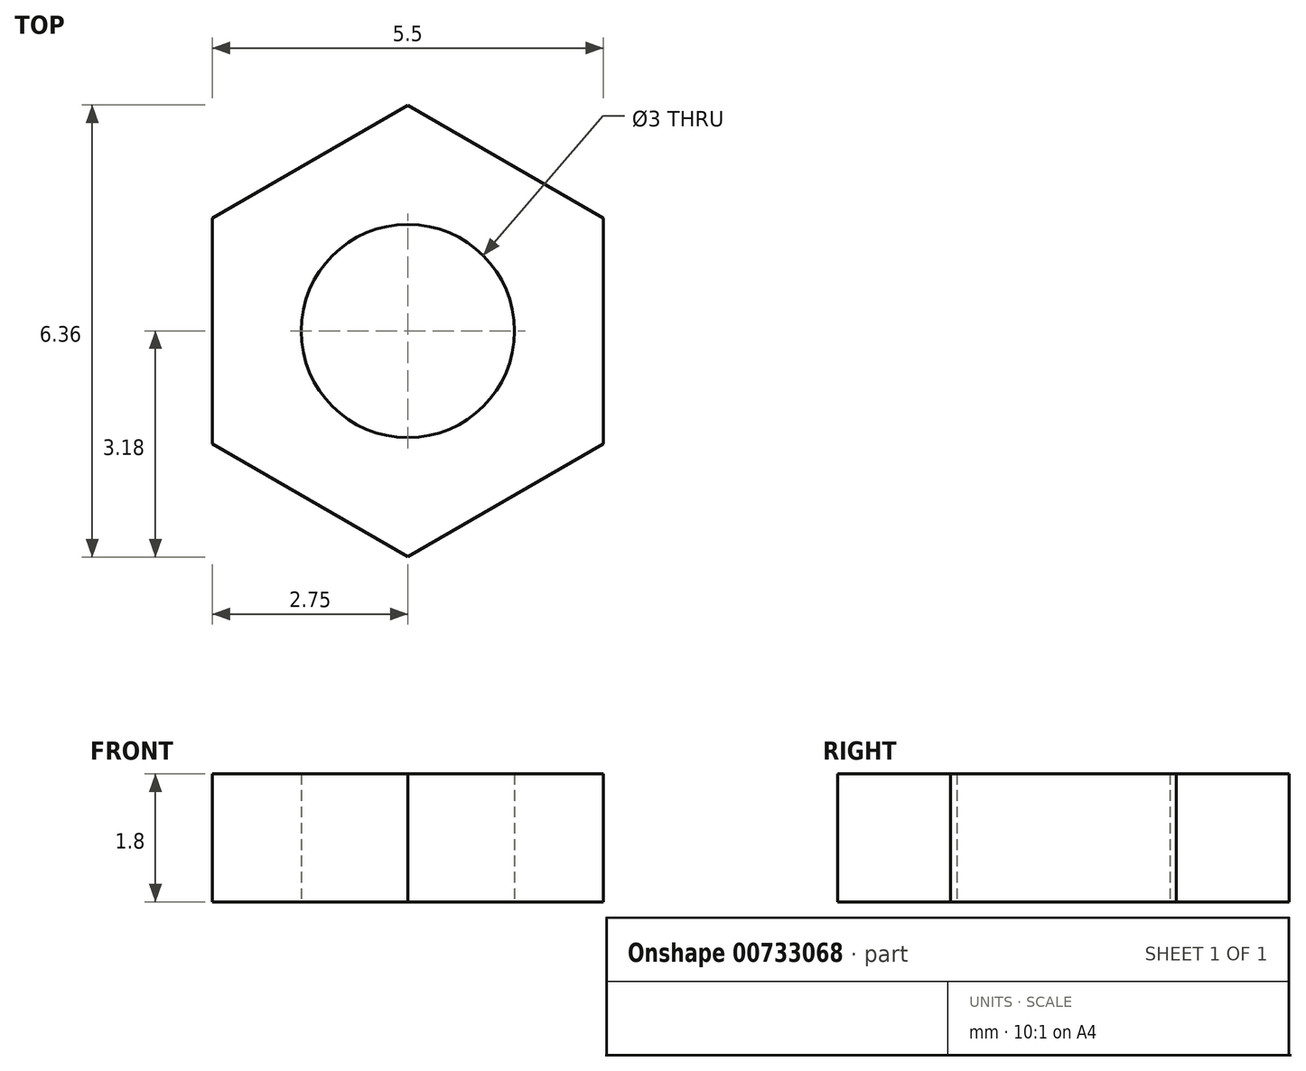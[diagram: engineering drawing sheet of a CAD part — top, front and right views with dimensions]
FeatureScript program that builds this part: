
annotation { "Feature Type Name" : "Feature", "Feature Type Description" : "" }
export const myFeature = defineFeature(function(context is Context, id is Id, definition is map)
    precondition{}
    {
        {
            var Q0;
            Q0=qCreatedBy(makeId("Top.planeOp"),FACE);
            var sketch = newSketch(context, id + "F0", { "sketchPlane" : qUnion([Q0])});
            skCircle(sketch, "E0.cCircle", {"center": v(0, 0) * mm, "radius": 2.75 * mm, "construction": true});
            skLineSegment(sketch, "E0.0", {"start": v(-2.75, 1.59) * mm, "end": v(0, 3.18) * mm});
            skLineSegment(sketch, "E0.1", {"start": v(0, 3.18) * mm, "end": v(2.75, 1.59) * mm});
            skLineSegment(sketch, "E0.2", {"start": v(2.75, 1.59) * mm, "end": v(2.75, -1.59) * mm});
            skLineSegment(sketch, "E0.3", {"start": v(2.75, -1.59) * mm, "end": v(0, -3.18) * mm});
            skLineSegment(sketch, "E0.4", {"start": v(0, -3.18) * mm, "end": v(-2.75, -1.59) * mm});
            skLineSegment(sketch, "E0.5", {"start": v(-2.75, -1.59) * mm, "end": v(-2.75, 1.59) * mm});
            skPoint(sketch, "E0.0.midPoint", {"position": v(-1.38, 2.38) * mm});
            skCircle(sketch, "E1", {"center": v(0, 0) * mm, "radius": 1.5 * mm});
            skSolve(sketch);
        }
        {
            var Q0;
            Q0=qSketchRegion(id+"F0",true);
            extrude(context, id + "F1", {"entities" : qUnion([Q0]), "depth" : 1.8 * mm, "offsetDistance" : 25 * mm});
        }
    });
